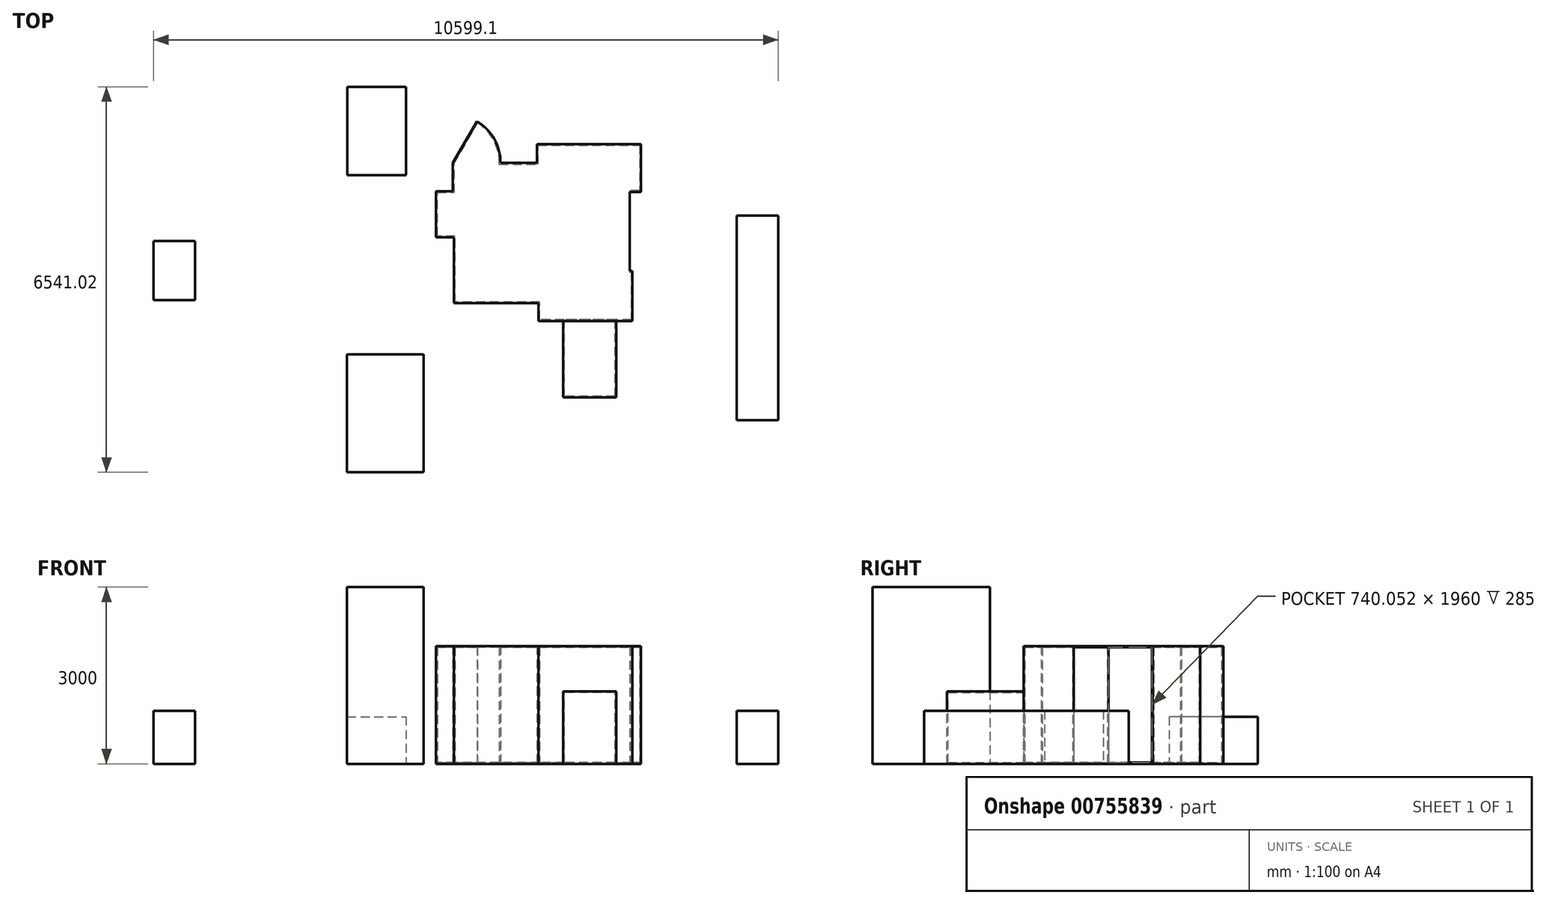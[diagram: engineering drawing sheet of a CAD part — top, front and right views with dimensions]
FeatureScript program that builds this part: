
annotation { "Feature Type Name" : "Feature", "Feature Type Description" : "" }
export const myFeature = defineFeature(function(context is Context, id is Id, definition is map)
    precondition{}
    {
        {
            var Q0;
            Q0=qCreatedBy(makeId("Top.planeOp"),FACE);
            var sketch = newSketch(context, id + "F0", { "sketchPlane" : qUnion([Q0])});
            skLineSegment(sketch, "E0.bottom", {"start": v(0, 6500) * mm, "end": v(5800, 6500) * mm});
            skLineSegment(sketch, "E0.left", {"start": v(0, 6500) * mm, "end": v(0, 0) * mm});
            skLineSegment(sketch, "E0.right", {"start": v(5800, 6500) * mm, "end": v(5800, 4485) * mm});
            skLineSegment(sketch, "E1", {"start": v(5800, 4485) * mm, "end": v(7450, 4485) * mm});
            skLineSegment(sketch, "E2", {"start": v(7450, 4485) * mm, "end": v(7450, 0) * mm});
            skLineSegment(sketch, "E3", {"start": v(5901.62, 0) * mm, "end": v(7450, 0) * mm});
            skLineSegment(sketch, "E4", {"start": v(0, 0) * mm, "end": v(1182.73, 0) * mm});
            skLineSegment(sketch, "E5", {"start": v(1182.73, 0) * mm, "end": v(5901.62, 0) * mm});
            skLineSegment(sketch, "E6", {"start": v(6750, 4485) * mm, "end": v(6750, 0) * mm, "construction": true});
            skLineSegment(sketch, "E7", {"start": v(5800, 4909.26) * mm, "end": v(6224.26, 4485) * mm});
            skSolve(sketch);
        }
        {
            var Q0;
            Q0=qCreatedBy(makeId("Top.planeOp"),FACE);
            var sketch = newSketch(context, id + "F1", { "sketchPlane" : qUnion([Q0])});
            skLineSegment(sketch, "E8", {"start": v(1930.66, 5379.02) * mm, "end": v(3355.66, 5379.02) * mm});
            skLineSegment(sketch, "E9", {"start": v(3355.66, 5379.02) * mm, "end": v(3355.66, 5698.6) * mm});
            skLineSegment(sketch, "E10", {"start": v(3355.66, 5698.6) * mm, "end": v(5120.66, 5698.6) * mm});
            skLineSegment(sketch, "E11", {"start": v(5120.66, 5698.6) * mm, "end": v(5120.66, 4889.13) * mm});
            skLineSegment(sketch, "E12", {"start": v(5120.66, 4889.13) * mm, "end": v(4932.26, 4889.13) * mm});
            skLineSegment(sketch, "E13", {"start": v(4932.26, 4889.13) * mm, "end": v(4932.26, 3549.47) * mm});
            skLineSegment(sketch, "E14", {"start": v(4932.26, 3549.47) * mm, "end": v(4979.5, 3549.47) * mm});
            skLineSegment(sketch, "E15", {"start": v(4979.5, 3549.47) * mm, "end": v(4979.5, 2698.6) * mm});
            skLineSegment(sketch, "E16", {"start": v(4979.5, 2698.6) * mm, "end": v(3380.27, 2698.6) * mm});
            skLineSegment(sketch, "E17", {"start": v(3380.27, 2698.6) * mm, "end": v(3380.27, 2998.6) * mm});
            skLineSegment(sketch, "E18", {"start": v(3380.27, 2998.6) * mm, "end": v(1948.93, 2998.6) * mm});
            skLineSegment(sketch, "E19", {"start": v(1948.93, 2998.6) * mm, "end": v(1948.93, 4119.09) * mm});
            skLineSegment(sketch, "E20", {"start": v(1948.93, 4119.09) * mm, "end": v(1645.66, 4119.09) * mm});
            skLineSegment(sketch, "E21", {"start": v(1645.66, 4119.09) * mm, "end": v(1645.66, 4899.14) * mm});
            skLineSegment(sketch, "E22", {"start": v(1645.66, 4899.14) * mm, "end": v(1930.66, 4899.14) * mm});
            skLineSegment(sketch, "E23", {"start": v(1930.66, 4899.14) * mm, "end": v(1930.66, 5379.02) * mm});
            skCircle(sketch, "E24", {"center": v(3936.17, 4198.8) * mm, "radius": 121.65 * mm});
            skLineSegment(sketch, "E25", {"start": v(1930.66, 5379.02) * mm, "end": v(2342.17, 6087.29) * mm});
            skArc(sketch, "E26", {"start": v(2739.37, 5379.02) * mm, "mid": v(2633.86, 5785.36) * mm, "end": v(2342.17, 6087.29) * mm});
            skSolve(sketch);
        }
        {
            var Q0;
            Q0 = qSketchRegion(id + "F1", true);
            var Q1;
            Q1=makeQuery(id+"F1.imprint","IMPRINT",FACE,{"disambiguationData":[TD([[makeQuery(id+"F1.imprint","IMPRINT",EDGE,{"derivedFrom":sQuery(id+"F1.wireOp",EDGE,"E24")}),1.0]])]});
            extrude(context, id + "F2", {"entities" : qUnion([Q0, Q1]), "depth" : 2000 * mm, "offsetDistance" : 25 * mm});
        }
        {
            var Q0;
            Q0=makeQuery(id+"F2.opExtrude","SWEPT_FACE",FACE,{"disambiguationData":[OSD([sQuery(id+"F1.wireOp",EDGE,"E16")])]});
            var sketch = newSketch(context, id + "F3", { "sketchPlane" : qUnion([Q0])});
            skLineSegment(sketch, "E27.bottom", {"start": v(4703.88, 0) * mm, "end": v(3803.24, 0) * mm});
            skLineSegment(sketch, "E27.top", {"start": v(4703.88, 1232.52) * mm, "end": v(3803.24, 1232.52) * mm});
            skLineSegment(sketch, "E27.left", {"start": v(4703.88, 0) * mm, "end": v(4703.88, 1232.52) * mm});
            skLineSegment(sketch, "E27.right", {"start": v(3803.24, 0) * mm, "end": v(3803.24, 1232.52) * mm});
            skSolve(sketch);
        }
        {
            var Q0;
            Q0=makeQuery(id+"F3.imprint","IMPRINT",FACE,{"disambiguationData":[TD([[makeQuery(id+"F3.imprint","IMPRINT",EDGE,{"derivedFrom":sQuery(id+"F3.wireOp",EDGE,"E27.bottom")}),-1.0]])]});
            extrude(context, id + "F4", {"entities" : qUnion([Q0]), "operationType" : NewBodyOperationType.ADD, "depth" : 1300 * mm, "offsetDistance" : 25 * mm});
        }
        {
            var Q0;
            Q0=qCreatedBy(makeId("Top.planeOp"),FACE);
            var sketch = newSketch(context, id + "F5", { "sketchPlane" : qUnion([Q0])});
            skLineSegment(sketch, "E28.bottom", {"start": v(130, 130) * mm, "end": v(1430, 130) * mm});
            skLineSegment(sketch, "E28.top", {"start": v(130, 2130) * mm, "end": v(1430, 2130) * mm});
            skLineSegment(sketch, "E28.left", {"start": v(130, 130) * mm, "end": v(130, 2130) * mm});
            skLineSegment(sketch, "E28.right", {"start": v(1430, 130) * mm, "end": v(1430, 2130) * mm});
            skSolve(sketch);
        }
        {
            var Q0;
            Q0 = qSketchRegion(id + "F5", true);
            extrude(context, id + "F6", {"entities" : qUnion([Q0]), "depth" : 3000 * mm, "offsetDistance" : 25 * mm});
        }
        {
            var Q0;
            Q0=qCreatedBy(makeId("Top.planeOp"),FACE);
            var sketch = newSketch(context, id + "F7", { "sketchPlane" : qUnion([Q0])});
            skLineSegment(sketch, "E29.0", {"start": v(7450, 4485) * mm, "end": v(7450, 0) * mm});
            skLineSegment(sketch, "E30.0", {"start": v(6750, 4485) * mm, "end": v(6750, 0) * mm});
            skLineSegment(sketch, "E31.bottom", {"start": v(7450, 4485) * mm, "end": v(6750, 4485) * mm});
            skLineSegment(sketch, "E31.top", {"start": v(7450, 1011.3) * mm, "end": v(6750, 1011.3) * mm});
            skLineSegment(sketch, "E31.left", {"start": v(7450, 4485) * mm, "end": v(7450, 1011.3) * mm});
            skLineSegment(sketch, "E31.right", {"start": v(6750, 4485) * mm, "end": v(6750, 1011.3) * mm});
            skSolve(sketch);
        }
        {
            var Q0;
            Q0=makeQuery(id+"F7.imprint","IMPRINT",FACE,{"disambiguationData":[TD([[makeQuery(id+"F7.imprint","IMPRINT",EDGE,{"derivedFrom":sQuery(id+"F7.wireOp",EDGE,"E31.bottom")}),1.0]])]});
            extrude(context, id + "F8", {"entities" : qUnion([Q0]), "depth" : 900 * mm, "offsetDistance" : 25 * mm});
        }
        {
            var Q0;
            Q0=qCreatedBy(makeId("Top.planeOp"),FACE);
            var sketch = newSketch(context, id + "F9", { "sketchPlane" : qUnion([Q0])});
            skLineSegment(sketch, "E32.bottom", {"start": v(136.6, 6671.02) * mm, "end": v(1136.6, 6671.02) * mm});
            skLineSegment(sketch, "E32.top", {"start": v(136.6, 5171.02) * mm, "end": v(1136.6, 5171.02) * mm});
            skLineSegment(sketch, "E32.left", {"start": v(136.6, 6671.02) * mm, "end": v(136.6, 5171.02) * mm});
            skLineSegment(sketch, "E32.right", {"start": v(1136.6, 6671.02) * mm, "end": v(1136.6, 5171.02) * mm});
            skSolve(sketch);
        }
        {
            var Q0;
            Q0 = qSketchRegion(id + "F9", true);
            extrude(context, id + "F10", {"entities" : qUnion([Q0]), "depth" : 800 * mm, "offsetDistance" : 25 * mm});
        }
        {
            var Q0;
            Q0=qCreatedBy(makeId("Top.planeOp"),FACE);
            var sketch = newSketch(context, id + "F11", { "sketchPlane" : qUnion([Q0])});
            skLineSegment(sketch, "E33.bottom", {"start": v(-3149.06, 4052.7) * mm, "end": v(-2449.06, 4052.7) * mm});
            skLineSegment(sketch, "E33.top", {"start": v(-3149.06, 3052.7) * mm, "end": v(-2449.06, 3052.7) * mm});
            skLineSegment(sketch, "E33.left", {"start": v(-3149.06, 4052.7) * mm, "end": v(-3149.06, 3052.7) * mm});
            skLineSegment(sketch, "E33.right", {"start": v(-2449.06, 4052.7) * mm, "end": v(-2449.06, 3052.7) * mm});
            skSolve(sketch);
        }
        {
            var Q0;
            Q0=makeQuery(id+"F11.imprint","IMPRINT",FACE,{"disambiguationData":[TD([[makeQuery(id+"F11.imprint","IMPRINT",EDGE,{"derivedFrom":sQuery(id+"F11.wireOp",EDGE,"E33.bottom")}),-1.0]])]});
            extrude(context, id + "F12", {"entities" : qUnion([Q0]), "depth" : 900 * mm, "offsetDistance" : 25 * mm});
        }
        {
            var Q0;
            Q0=makeQuery(id+"F2.opExtrude","SWEPT_FACE",FACE,{"disambiguationData":[OSD([sQuery(id+"F1.wireOp",EDGE,"E13")])]});
            shell(context, id + "F13", {"entities" : qUnion([Q0]), "thickness" : 20 * mm});
        }
    });
